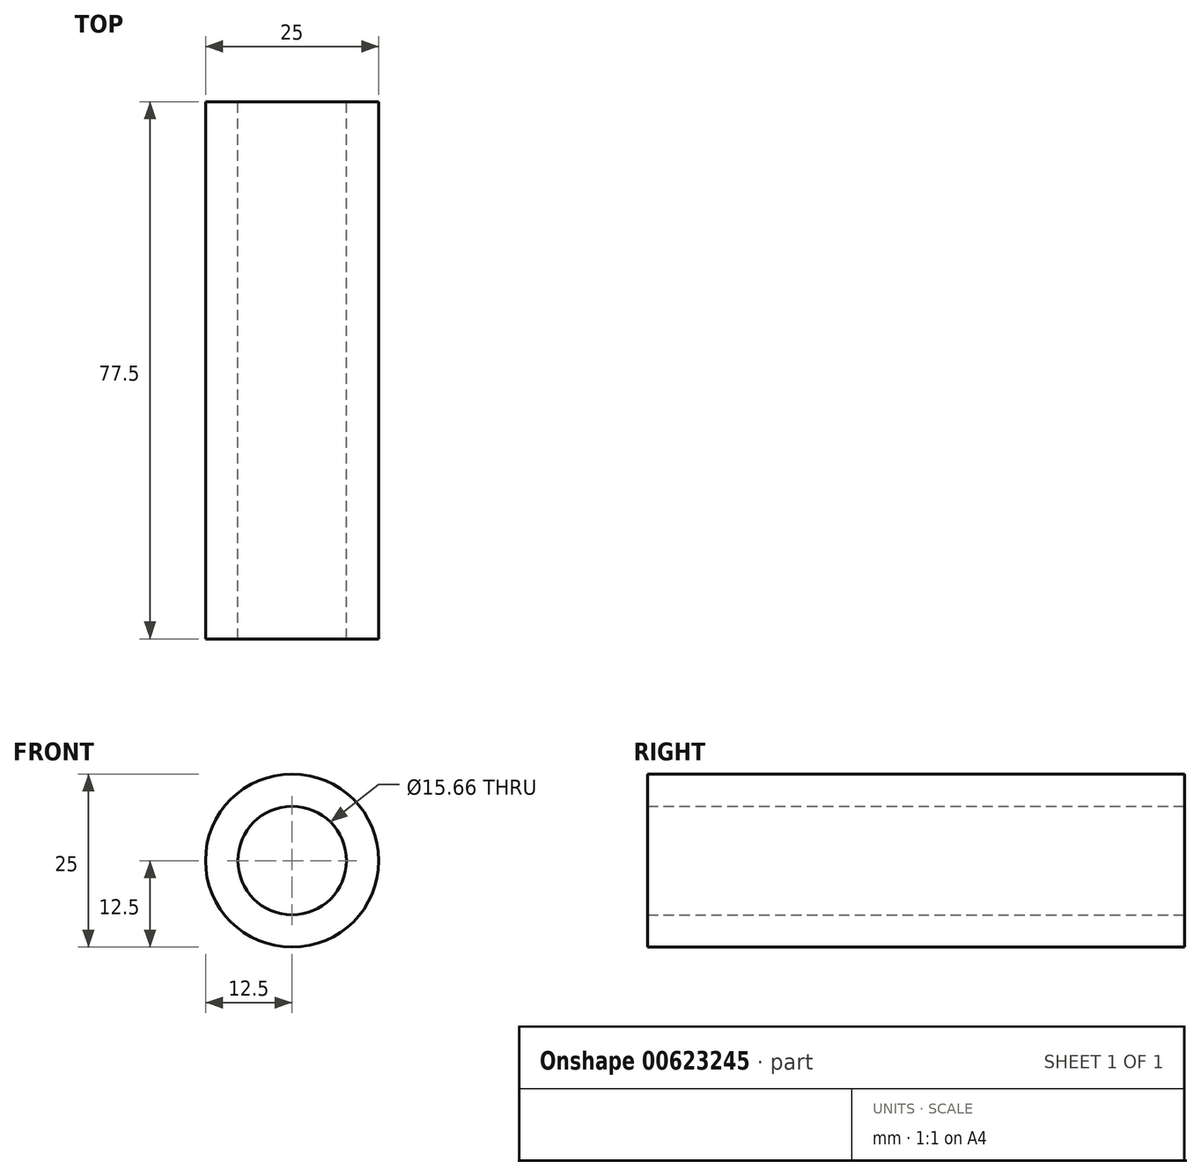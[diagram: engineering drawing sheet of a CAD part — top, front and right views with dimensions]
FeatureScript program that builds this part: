
annotation { "Feature Type Name" : "Feature", "Feature Type Description" : "" }
export const myFeature = defineFeature(function(context is Context, id is Id, definition is map)
    precondition{}
    {
        {
            var Q0;
            Q0=qCreatedBy(makeId("Front.planeOp"),FACE);
            var sketch = newSketch(context, id + "F0", { "sketchPlane" : qUnion([Q0])});
            skCircle(sketch, "E0", {"center": v(0, 0) * mm, "radius": 12.5 * mm});
            skCircle(sketch, "E1", {"center": v(0, 0) * mm, "radius": 7.83 * mm});
            skSolve(sketch);
        }
        {
            var Q0;
            Q0 = qSketchRegion(id + "F0", true);
            extrude(context, id + "F1", {"entities" : qUnion([Q0]), "depth" : 77.5 * mm, "offsetDistance" : 25 * mm});
        }
    });
